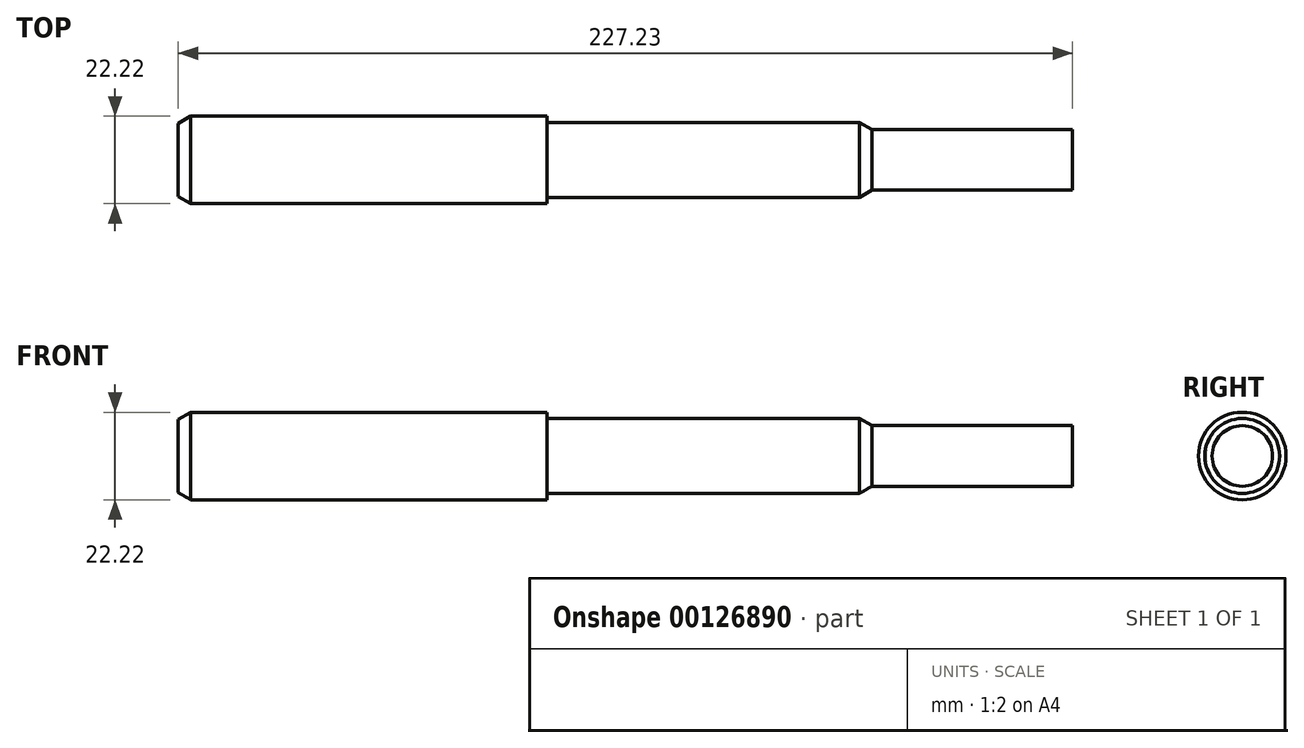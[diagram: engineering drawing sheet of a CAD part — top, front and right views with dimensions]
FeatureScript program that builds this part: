
annotation { "Feature Type Name" : "Feature", "Feature Type Description" : "" }
export const myFeature = defineFeature(function(context is Context, id is Id, definition is map)
    precondition{}
    {
        {
            var Q0;
            Q0=qCreatedBy(makeId("Right.planeOp"),FACE);
            var sketch = newSketch(context, id + "F0", { "sketchPlane" : qUnion([Q0])});
            skCircle(sketch, "E0", {"center": v(0, 0) * mm, "radius": 11.11 * mm});
            skCircle(sketch, "E1", {"center": v(0, 0) * mm, "radius": 9.53 * mm});
            skSolve(sketch);
        }
        {
            var Q0;
            Q0=qSketchRegion(id+"F0",true);
            var Q1;
            Q1=makeQuery(id+"F0.imprint","IMPRINT",FACE,{"disambiguationData":[TD([[makeQuery(id+"F0.imprint","IMPRINT",EDGE,{"derivedFrom":sQuery(id+"F0.wireOp",EDGE,"E1")}),1.0]])]});
            extrude(context, id + "F1", {"entities" : qUnion([Q0, Q1]), "oppositeDirection" : true, "depth" : 93.68 * mm});
        }
        {
            var Q0;
            Q0=makeQuery(id+"F0.imprint","IMPRINT",FACE,{"disambiguationData":[TD([[makeQuery(id+"F0.imprint","IMPRINT",EDGE,{"derivedFrom":sQuery(id+"F0.wireOp",EDGE,"E1")}),1.0]])]});
            extrude(context, id + "F2", {"entities" : qUnion([Q0]), "depth" : 82.55 * mm});
        }
        {
            var Q0;
            Q0=makeQuery(id+"F1.opExtrude","CAP_EDGE",EDGE,{"disambiguationData":[OSD([sQuery(id+"F0.wireOp",EDGE,"E0")])],"isStart":false});
            chamfer(context, id + "F3", {"entities" : qUnion([Q0]), "chamferType" : ChamferType.OFFSET_ANGLE, "width" : 3.17 * mm, "oppositeDirection" : false, "angle" : 30 * degree, "tangentPropagation" : true});
        }
        {
            var Q0;
            Q0=makeQuery(id+"F2.opExtrude","CAP_EDGE",EDGE,{"disambiguationData":[OSD([sQuery(id+"F0.wireOp",EDGE,"E1")])],"isStart":false});
            chamfer(context, id + "F4", {"entities" : qUnion([Q0]), "chamferType" : ChamferType.OFFSET_ANGLE, "width" : 3.17 * mm, "oppositeDirection" : true, "angle" : 30 * degree, "tangentPropagation" : true});
        }
        {
            var Q0;
            Q0=makeQuery(id+"F2.opExtrude","CAP_FACE",FACE,{"disambiguationData":[OSD([sQuery(id+"F0.wireOp",EDGE,"E1")])],"isStart":false});
            extrude(context, id + "F5", {"entities" : qUnion([Q0]), "operationType" : NewBodyOperationType.ADD, "depth" : 51 * mm});
        }
    });
